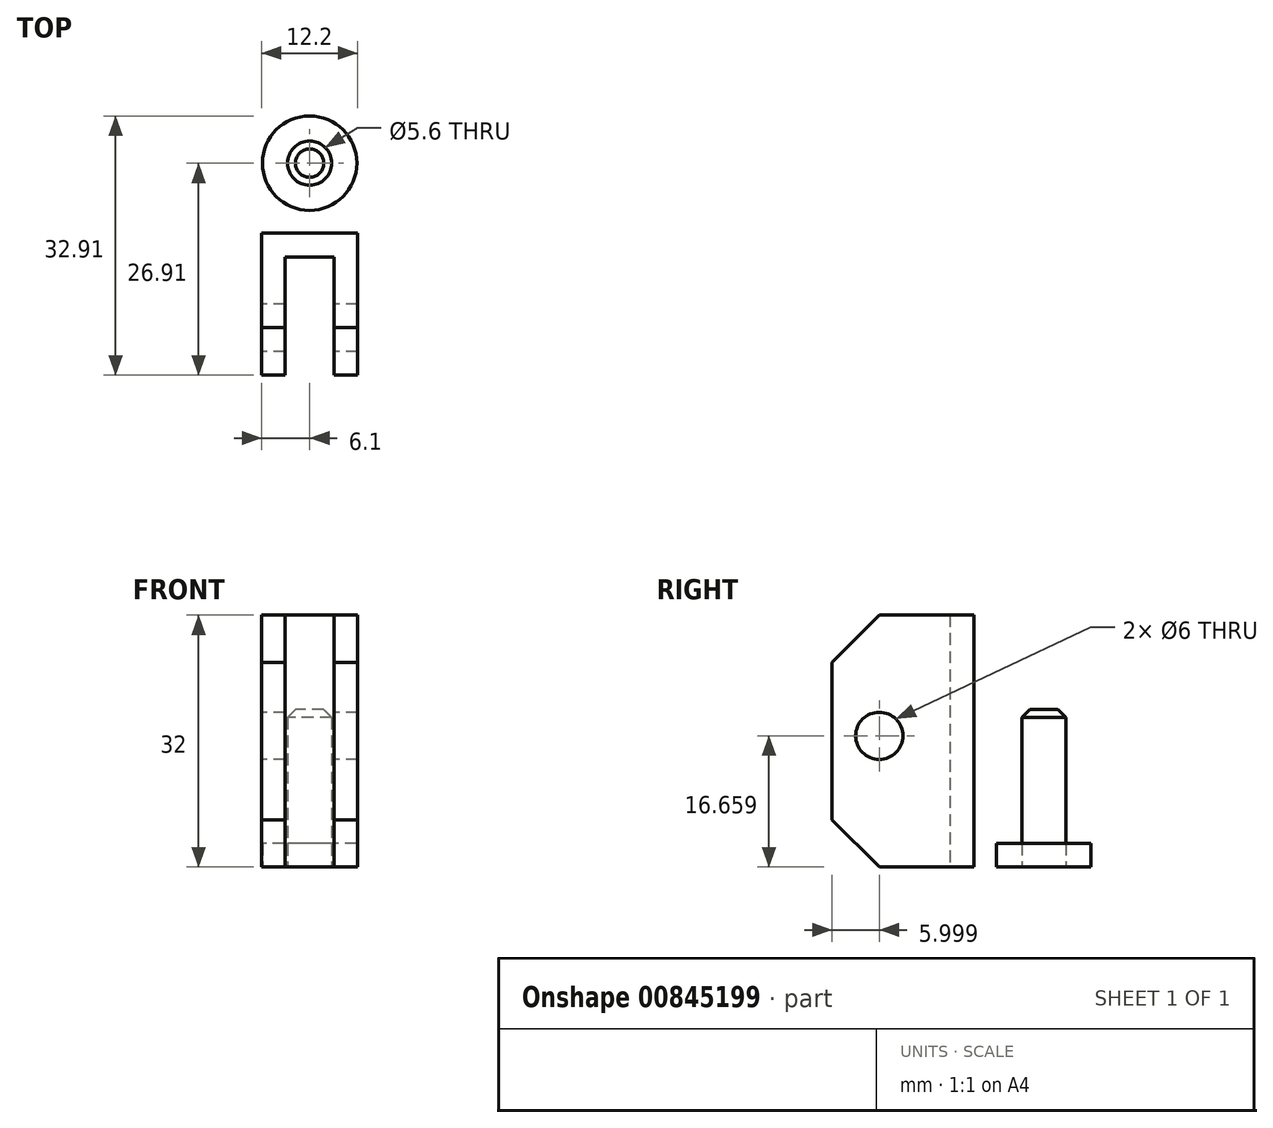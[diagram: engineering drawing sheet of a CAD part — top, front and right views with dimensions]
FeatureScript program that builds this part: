
annotation { "Feature Type Name" : "Feature", "Feature Type Description" : "" }
export const myFeature = defineFeature(function(context is Context, id is Id, definition is map)
    precondition{}
    {
        {
            var Q0;
            Q0=qCreatedBy(makeId("Top.planeOp"),FACE);
            var sketch = newSketch(context, id + "F0", { "sketchPlane" : qUnion([Q0])});
            skCircle(sketch, "E0", {"center": v(0, 0) * mm, "radius": 2.8 * mm});
            skCircle(sketch, "E1", {"center": v(0, 0) * mm, "radius": 6 * mm});
            skLineSegment(sketch, "E2.bottom", {"start": v(-3.1, -11.91) * mm, "end": v(3.1, -11.91) * mm});
            skLineSegment(sketch, "E2.top", {"start": v(-3.1, -8.91) * mm, "end": v(3.1, -8.91) * mm});
            skLineSegment(sketch, "E2.left", {"start": v(-3.1, -11.91) * mm, "end": v(-3.1, -8.91) * mm});
            skLineSegment(sketch, "E2.right", {"start": v(3.1, -11.91) * mm, "end": v(3.1, -8.91) * mm});
            skPoint(sketch, "E2.middle", {"position": v(0, -10.41) * mm});
            skLineSegment(sketch, "E3.bottom", {"start": v(-3.1, -8.91) * mm, "end": v(-6.1, -8.91) * mm});
            skLineSegment(sketch, "E3.top", {"start": v(-3.1, -26.91) * mm, "end": v(-6.1, -26.91) * mm});
            skLineSegment(sketch, "E3.left", {"start": v(-3.1, -8.91) * mm, "end": v(-3.1, -26.91) * mm});
            skLineSegment(sketch, "E3.right", {"start": v(-6.1, -8.91) * mm, "end": v(-6.1, -26.91) * mm});
            skLineSegment(sketch, "E4.bottom", {"start": v(3.1, -8.91) * mm, "end": v(6.1, -8.91) * mm});
            skLineSegment(sketch, "E4.top", {"start": v(3.1, -26.91) * mm, "end": v(6.1, -26.91) * mm});
            skLineSegment(sketch, "E4.left", {"start": v(3.1, -8.91) * mm, "end": v(3.1, -26.91) * mm});
            skLineSegment(sketch, "E4.right", {"start": v(6.1, -8.91) * mm, "end": v(6.1, -26.91) * mm});
            skSolve(sketch);
        }
        {
            var Q0;
            Q0=makeQuery(id+"F0.imprint","IMPRINT",FACE,{"disambiguationData":[TD([[makeQuery(id+"F0.imprint","IMPRINT",EDGE,{"derivedFrom":sQuery(id+"F0.wireOp",EDGE,"E0")}),-1.0]])]});
            var Q1;
            Q1=sQuery(id+"F0.wireOp",EDGE,"E1");
            extrude(context, id + "F1", {"entities" : qUnion([Q0]), "surfaceEntities" : qUnion([Q1]), "depth" : 3 * mm, "offsetDistance" : 25 * mm});
        }
        {
            var Q0;
            Q0=makeQuery(id+"F0.imprint","IMPRINT",FACE,{"disambiguationData":[TD([[makeQuery(id+"F0.imprint","IMPRINT",EDGE,{"derivedFrom":sQuery(id+"F0.wireOp",EDGE,"E0")}),1.0]])]});
            extrude(context, id + "F2", {"entities" : qUnion([Q0]), "depth" : 20 * mm, "offsetDistance" : 25 * mm});
        }
        {
            var Q0;
            Q0=makeQuery(id+"F2.opExtrude","CAP_EDGE",EDGE,{"disambiguationData":[OSD([sQuery(id+"F0.wireOp",EDGE,"E0")])],"isStart":false});
            chamfer(context, id + "F3", {"entities" : qUnion([Q0]), "width" : 1 * mm, "tangentPropagation" : true});
        }
        {
            var Q0;
            {var subQ3=sQuery(id+"F0.wireOp",EDGE,"E4.bottom");Q0=makeQuery(id+"F0.imprint","IMPRINT",FACE,{"disambiguationData":[TD([[makeQuery(id+"F0.imprint","IMPRINT",EDGE,{"derivedFrom":subQ3}),-1.0]])]});}
            var Q1;
            {var subQ0=sQuery(id+"F0.wireOp",EDGE,"E2.bottom");Q1=makeQuery(id+"F0.imprint","IMPRINT",FACE,{"disambiguationData":[TD([[makeQuery(id+"F0.imprint","IMPRINT",EDGE,{"derivedFrom":subQ0}),1.0]])]});}
            var Q2;
            {var subQ3=sQuery(id+"F0.wireOp",EDGE,"E3.bottom");Q2=makeQuery(id+"F0.imprint","IMPRINT",FACE,{"disambiguationData":[TD([[makeQuery(id+"F0.imprint","IMPRINT",EDGE,{"derivedFrom":subQ3}),1.0]])]});}
            extrude(context, id + "F4", {"entities" : qUnion([Q0, Q1, Q2]), "depth" : 32 * mm, "offsetDistance" : 25 * mm});
        }
        {
            var Q0;
            Q0=makeQuery(id+"F4.opExtrude","SWEPT_FACE",FACE,{"disambiguationData":[OSD([sQuery(id+"F0.wireOp",EDGE,"E3.right")])]});
            var sketch = newSketch(context, id + "F5", { "sketchPlane" : qUnion([Q0])});
            skLineSegment(sketch, "E5.0", {"start": v(11.91, 32) * mm, "end": v(11.91, 0) * mm, "construction": true});
            skLineSegment(sketch, "E6", {"start": v(20.91, 32) * mm, "end": v(20.91, 0) * mm, "construction": true});
            skCircle(sketch, "E7", {"center": v(20.91, 16.66) * mm, "radius": 3 * mm});
            skSolve(sketch);
        }
        {
            var Q0;
            Q0=makeQuery(id+"F5.imprint","IMPRINT",FACE,{"disambiguationData":[TD([[makeQuery(id+"F5.imprint","IMPRINT",EDGE,{"derivedFrom":sQuery(id+"F5.wireOp",EDGE,"E7")}),1.0]])]});
            extrude(context, id + "F6", {"entities" : qUnion([Q0]), "operationType" : NewBodyOperationType.REMOVE, "oppositeDirection" : true, "depth" : 25 * mm, "offsetDistance" : 25 * mm});
        }
        {
            var Q0;
            Q0=makeQuery(id+"F4.opExtrude","CAP_EDGE",EDGE,{"disambiguationData":[OSD([sQuery(id+"F0.wireOp",EDGE,"E3.top")])],"isStart":false});
            var Q1;
            Q1=makeQuery(id+"F4.opExtrude","CAP_EDGE",EDGE,{"disambiguationData":[OSD([sQuery(id+"F0.wireOp",EDGE,"E4.top")])],"isStart":false});
            var Q2;
            Q2=makeQuery(id+"F4.opExtrude","CAP_EDGE",EDGE,{"disambiguationData":[OSD([sQuery(id+"F0.wireOp",EDGE,"E3.top")])],"isStart":true});
            var Q3;
            Q3=makeQuery(id+"F4.opExtrude","CAP_EDGE",EDGE,{"disambiguationData":[OSD([sQuery(id+"F0.wireOp",EDGE,"E4.top")])],"isStart":true});
            chamfer(context, id + "F7", {"entities" : qUnion([Q0, Q1, Q2, Q3]), "width" : 6 * mm, "tangentPropagation" : true});
        }
    });
